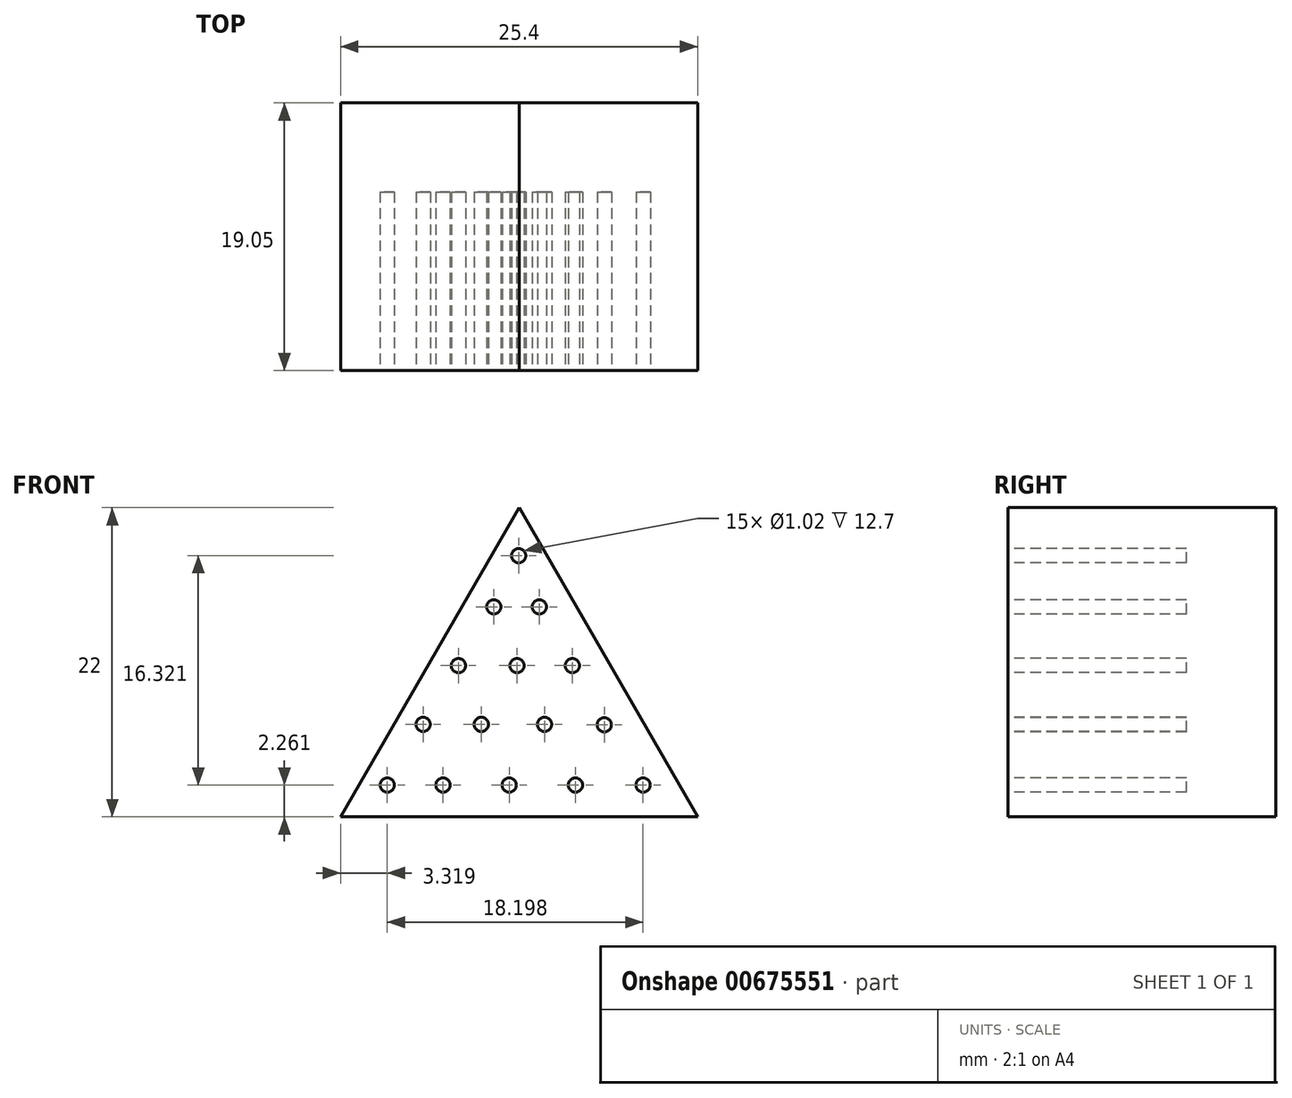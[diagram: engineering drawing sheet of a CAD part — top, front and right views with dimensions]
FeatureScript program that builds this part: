
annotation { "Feature Type Name" : "Feature", "Feature Type Description" : "" }
export const myFeature = defineFeature(function(context is Context, id is Id, definition is map)
    precondition{}
    {
        {
            var Q0;
            Q0=qCreatedBy(makeId("Front.planeOp"),FACE);
            var sketch = newSketch(context, id + "F0", { "sketchPlane" : qUnion([Q0])});
            skLineSegment(sketch, "E0", {"start": v(-22.21, -22) * mm, "end": v(3.19, -22) * mm});
            skLineSegment(sketch, "E1", {"start": v(-22.21, -22) * mm, "end": v(-9.51, 0) * mm});
            skLineSegment(sketch, "E2", {"start": v(-9.51, 0) * mm, "end": v(3.19, -22) * mm});
            skSolve(sketch);
        }
        {
            var Q0;
            Q0 = qSketchRegion(id + "F0", true);
            extrude(context, id + "F1", {"entities" : qUnion([Q0]), "depth" : 19.05 * mm, "offsetDistance" : 25.4 * mm});
        }
        {
            var Q0;
            Q0=makeQuery(id+"F1.opExtrude","CAP_FACE",FACE,{"disambiguationData":[OSD([sQuery(id+"F0.wireOp",EDGE,"E0"),sQuery(id+"F0.wireOp",EDGE,"E1"),sQuery(id+"F0.wireOp",EDGE,"E2")])],"isStart":false});
            var sketch = newSketch(context, id + "F2", { "sketchPlane" : qUnion([Q0])});
            skCircle(sketch, "E3", {"center": v(-18.9, -19.74) * mm, "radius": 0.5 * mm});
            skCircle(sketch, "E4", {"center": v(-14.93, -19.74) * mm, "radius": 0.5 * mm});
            skCircle(sketch, "E5", {"center": v(-5.5, -19.74) * mm, "radius": 0.5 * mm});
            skCircle(sketch, "E6", {"center": v(-0.7, -19.74) * mm, "radius": 0.5 * mm});
            skCircle(sketch, "E7", {"center": v(-10.22, -19.74) * mm, "radius": 0.5 * mm});
            skCircle(sketch, "E8", {"center": v(-12.2, -15.42) * mm, "radius": 0.5 * mm});
            skCircle(sketch, "E9", {"center": v(-7.7, -15.42) * mm, "radius": 0.5 * mm});
            skCircle(sketch, "E10", {"center": v(-3.46, -15.46) * mm, "radius": 0.5 * mm});
            skCircle(sketch, "E11", {"center": v(-8.08, -7.06) * mm, "radius": 0.5 * mm});
            skCircle(sketch, "E12", {"center": v(-13.83, -11.24) * mm, "radius": 0.5 * mm});
            skCircle(sketch, "E13", {"center": v(-5.72, -11.24) * mm, "radius": 0.5 * mm});
            skCircle(sketch, "E14", {"center": v(-9.54, -3.42) * mm, "radius": 0.5 * mm});
            skCircle(sketch, "E15", {"center": v(-11.31, -7.06) * mm, "radius": 0.5 * mm});
            skCircle(sketch, "E16", {"center": v(-9.66, -11.24) * mm, "radius": 0.5 * mm});
            skCircle(sketch, "E17", {"center": v(-16.34, -15.42) * mm, "radius": 0.5 * mm});
            skSolve(sketch);
        }
        {
            var Q0;
            Q0 = qSketchRegion(id + "F2", true);
            extrude(context, id + "F3", {"entities" : qUnion([Q0]), "operationType" : NewBodyOperationType.REMOVE, "oppositeDirection" : true, "depth" : 12.7 * mm, "offsetDistance" : 25.4 * mm});
        }
    });
